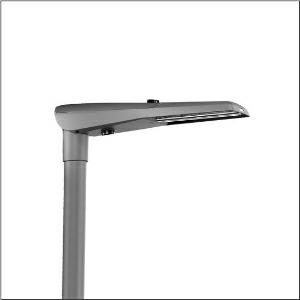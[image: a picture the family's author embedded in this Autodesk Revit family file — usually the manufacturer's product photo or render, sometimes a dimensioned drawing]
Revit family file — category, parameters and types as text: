
# Revit family: streetlight_sl_11_iq_mini___st1_2a_5xc2ac1y08ge_2c74
name_source: partatom
category: Lighting Fixtures
units: mm (PartAtom-declared; Revit-internal decimal feet)

## family parameters
Cut with Voids When Loaded = No
Host = Face
Light Source = No
Part Type = Normal
Room Calculation Point = No
Round Connector Dimension = Use Diameter
Shared = No

## types (1)
- --- (1 x LED, 3040 lm, 25.3 W, 2200K)
    Apparent Load = 25 VA
    CIE Flux Codes = 32 70 96 100 100
    Color Rendering = 70
    Color Temperature = 2200K
    Default Elevation = 1800 mm
    Description = Streetlight SL 11 iQ mini, mast luminaire, primary light control with 3 zone facetted reflector, of plastic, silver coated, highly specular, primary optical cover: cover, of PMMA, transparent, light distribution: ST1.2a, light emission: direct distribution, primary light characteristic: asymmetric, installation type: post-top, side-entry, lamps: LED, High Power LED, rated values: 3.570lm | 24,9W | 143,4lm/W (begin service life); end service life: 3.570lm | 25,7W; at 50% lumin. flux: 1.785lm | 12,8W | 139,5lm/W, colour temperature: 2200/2700/3000/4000K, colour rendering: CRI > 70, light colour: 722/727/730/740, light setting 1 begin service life: 100% | 3.570lm | 24,9W | 143,4lm/W | 3.000K, light setting 1 end service life: 25,7W, further light settings possible, control: pre-setting: logarithmic dimming characteristic, Street-Remote, Auto-Match, Temp-Guard, Lumen-Switch, Night-Set, Smart-Wire, Light-Fading, Desk-Remote (wireless, voltage-free reading and setting of iQ features in the workshop via application-optimized NFC function/RFID function), optimised constant luminous flux control (CLO 2.0), with cable H07RN-F 3x 1.5mm², mains connection: 230..240V, AC, 50/60Hz, connection cable pre-assembled, cable length: 6,5m, luminaire housing, of diecast aluminium, powder-coated, SITECO metallic grey (DB 702S), please order mast flange separately, inclination adjustable without tools: 0°, 5°, 10°, 15° (post-top) | 0°, -5°, -10°, -15° (side-entry), sealing non-destructively replaceable, multi-level sealing system, length: 736mm, width: 174mm, height: 116mm, mast flange for spigot size: 42mm (side-entry): 5XC10008XM4, 60/48mm (side-entry/post-top): 5XC10108XM2, 76/60mm (side-entry/post-top): 5XC10108XM1, equipment: standard, Smart Interface below and above, protection rating (complete): IP66, insulation class (complete): insulation class II (safety insulation), certification: CE, ENEC, ENEC+, VDE, UKCA, impact resistance: IK10, permissible operating ambient temperature for outdoor applications: -25..+50°C, standard-compliant lighting for roads and squares, Environmental Product Declaration (EPD) tested and certified by an independent institute, packaging unit: 1 piece

Light Distribution: ST1.2a
    Height = 116 mm
    Lamp = 1 x LED
    Lamp Light Flux = 3040 lm
    Lamp Power = 25.3 W
    Lamp count = 1
    Length = 736 mm
    Luminous efficacy = 120 lm/W
    Manufacturer = Siteco
    ModVariant = No
    Model = 5XC2AC1Y08GE
    Number of Poles = 1
    OnlyDefault = Yes
    Power Factor = 1
    Product Name = Streetlight SL 11 iQ mini | ST1.2a
    Product group = mast luminaire | pylon top
    ProductGroupID = 6100
    Protection Class = Protection class II
    Protection Degree = IP 66
    RLX_Detail_Level = 1
    RLX_Emergency_Light_Flux = 0 lm
    RLX_Emergency_Type = 0
    RLX_Emergency_Type_DB = No
    RlxData = <blob elided: 53757 chars, md5=2578ac4a>
    Socket = socket
    Standby Power = 0 W
    System Light Flux = 3040 lm
    System Power = 25 W
    Type Comments = individual setting: luminous flux: 100 % | dim-lin: 254 | 351 mA
    Type Image = l_1006751.jpg
    URL = http://relux.com
    VarID = @adj_042079
    Voltage = 0 V
    Weight = 0.00 kg
    Width = 174 mm

## geometry (parser evidence)
native form markers: Blend x4, Sweep x10
no freeform markers — native parametric forms only
